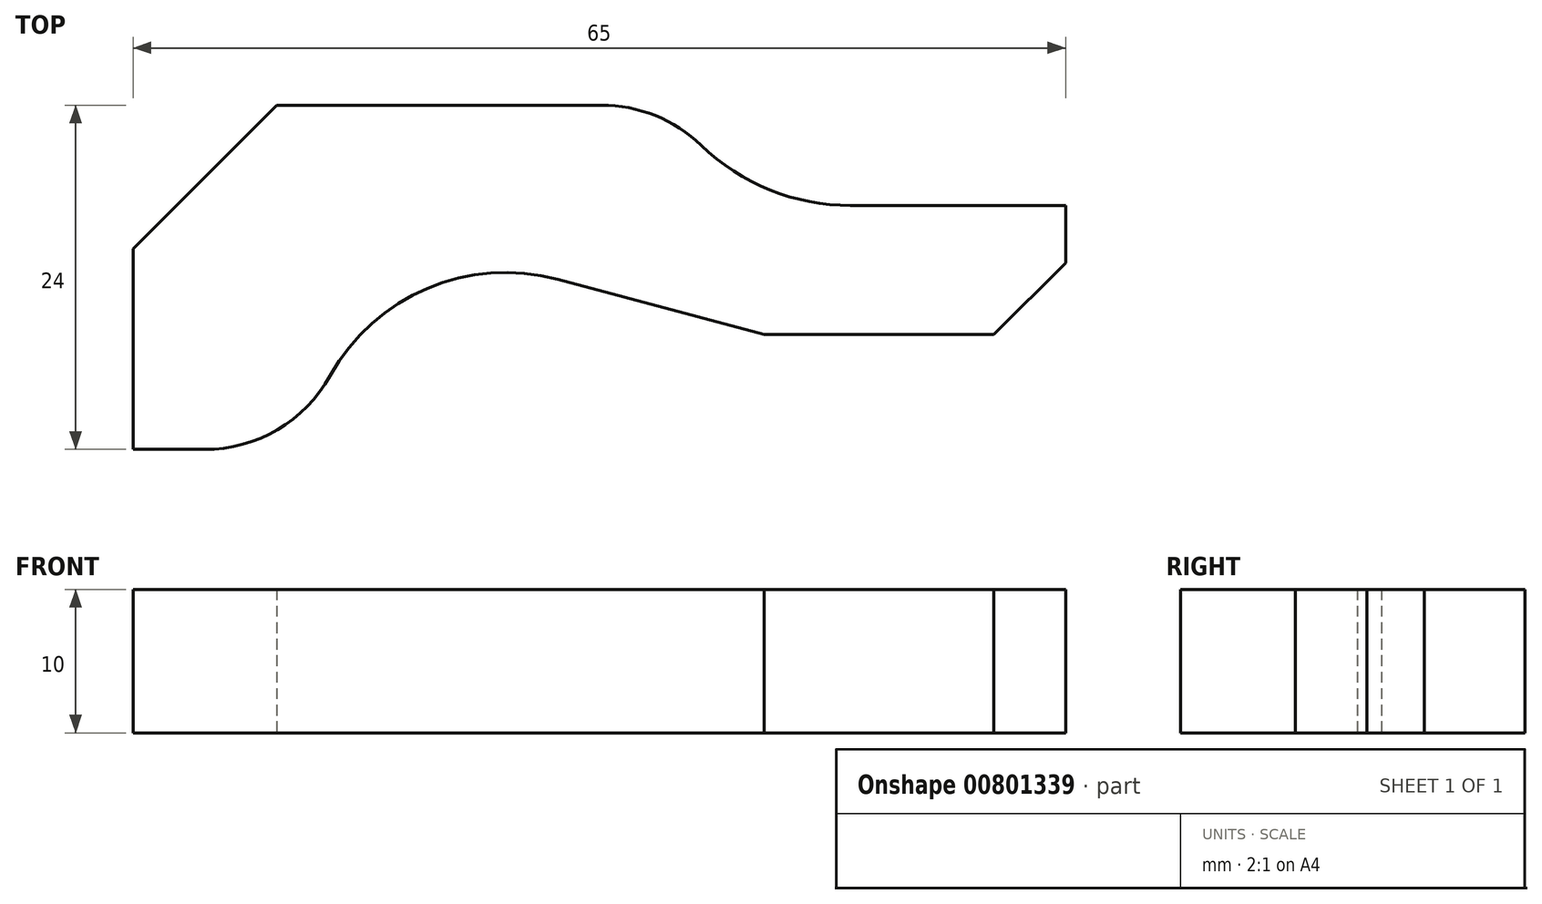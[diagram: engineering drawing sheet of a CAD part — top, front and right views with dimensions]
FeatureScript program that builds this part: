
annotation { "Feature Type Name" : "Feature", "Feature Type Description" : "" }
export const myFeature = defineFeature(function(context is Context, id is Id, definition is map)
    precondition{}
    {
        {
            var Q0;
            Q0=qCreatedBy(makeId("Top.planeOp"),FACE);
            var sketch = newSketch(context, id + "F0", { "sketchPlane" : qUnion([Q0])});
            skLineSegment(sketch, "E0", {"start": v(0, 0) * mm, "end": v(0, 14) * mm});
            skLineSegment(sketch, "E1", {"start": v(0, 14) * mm, "end": v(10, 24) * mm});
            skLineSegment(sketch, "E2", {"start": v(10, 24) * mm, "end": v(32.65, 24) * mm});
            skArc(sketch, "E3", {"start": v(32.65, 24) * mm, "mid": v(36.4, 23.27) * mm, "end": v(39.6, 21.2) * mm});
            skArc(sketch, "E4", {"start": v(39.6, 21.2) * mm, "mid": v(44.39, 18.09) * mm, "end": v(50, 17) * mm});
            skLineSegment(sketch, "E5", {"start": v(50, 17) * mm, "end": v(65, 17) * mm});
            skLineSegment(sketch, "E6", {"start": v(65, 17) * mm, "end": v(65, 13) * mm});
            skLineSegment(sketch, "E7", {"start": v(65, 13) * mm, "end": v(60, 8) * mm});
            skLineSegment(sketch, "E8", {"start": v(60, 8) * mm, "end": v(44, 8) * mm});
            skLineSegment(sketch, "E9", {"start": v(44, 8) * mm, "end": v(29.6, 11.86) * mm});
            skArc(sketch, "E10", {"start": v(29.6, 11.86) * mm, "mid": v(20.51, 11.23) * mm, "end": v(13.74, 5.14) * mm});
            skArc(sketch, "E11", {"start": v(13.74, 5.14) * mm, "mid": v(10.07, 1.38) * mm, "end": v(5, 0) * mm});
            skLineSegment(sketch, "E12", {"start": v(5, 0) * mm, "end": v(0, 0) * mm});
            skSolve(sketch);
        }
        {
            var Q0;
            Q0=makeQuery(id+"F0.imprint","IMPRINT",FACE,{"disambiguationData":[TD([[makeQuery(id+"F0.imprint","IMPRINT",EDGE,{"derivedFrom":sQuery(id+"F0.wireOp",EDGE,"E0")}),-1.0]])]});
            extrude(context, id + "F1", {"entities" : qUnion([Q0]), "depth" : 10 * mm, "offsetDistance" : 25 * mm});
        }
    });
